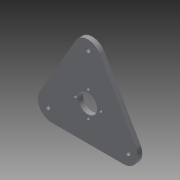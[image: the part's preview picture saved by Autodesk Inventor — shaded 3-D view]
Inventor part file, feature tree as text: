
AUTODESK INVENTOR PART (.ipt)
format: ipt  version: 2013 (Build 170138000, 138)  size: 102,400 bytes
history: native  units: in
note: dims shown in document units (in); Inventor stores cm internally (conversion verified against a paired STEP export)
features: extrude x1, fillet x1, sketch x1
ambient origin geometry x8: Origin, YZ Plane, XZ Plane, XY Plane, X Axis, Y Axis, Z Axis, Center Point
bodies: Solid1 (feature_tree)
feature tree (3):
  extrude  "Extrusion1"  Depth=0.25in
  fillet  "Fillet1"  Radius=2.5in
  sketch  "Sketch2"  dims[d0=0.3125in d1=0.25in d2=2.5in d3=1.1811in d5=360.0deg d8=0.5in d9=0.5in d10=0.5in d11=0.25in d12=0.0in d13=0.75in d14=1.378in d15=0.1772in d16=1.5748in d18=360.0deg d20=1.02in]
